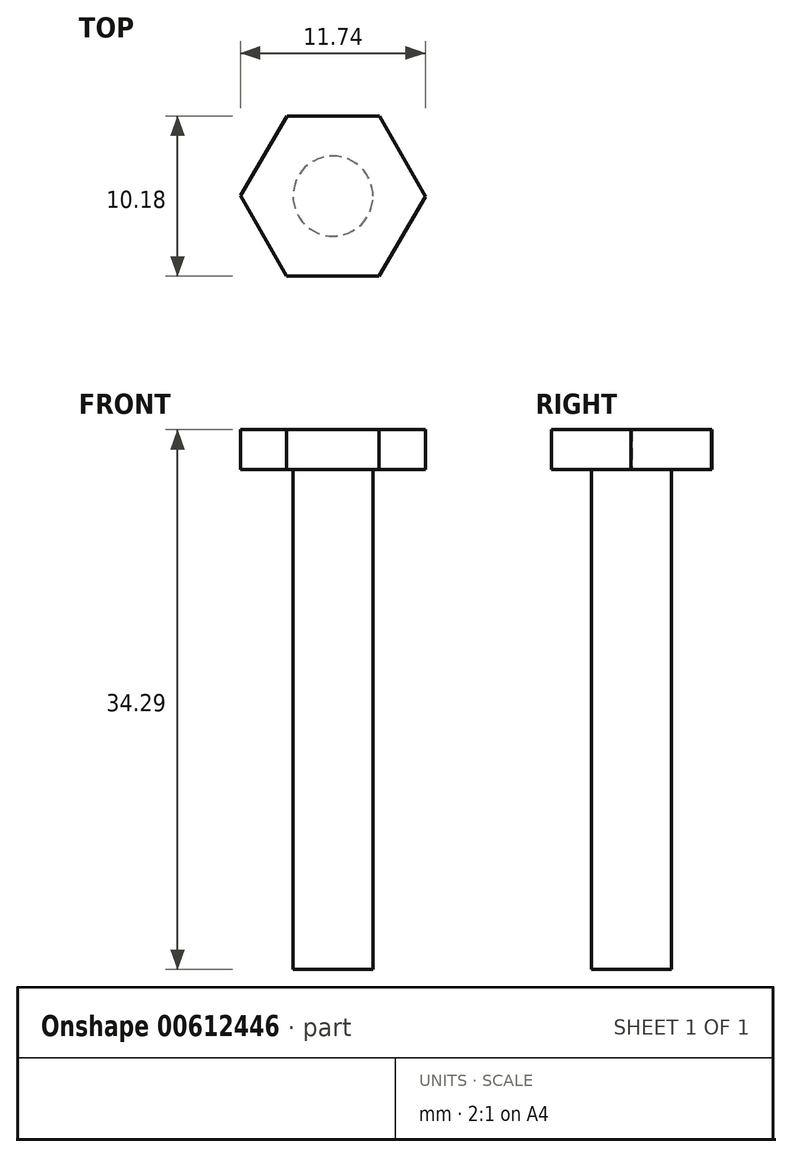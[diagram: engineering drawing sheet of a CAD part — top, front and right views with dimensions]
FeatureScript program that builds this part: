
annotation { "Feature Type Name" : "Feature", "Feature Type Description" : "" }
export const myFeature = defineFeature(function(context is Context, id is Id, definition is map)
    precondition{}
    {
        {
            var Q0;
            Q0=qCreatedBy(makeId("Top.planeOp"),FACE);
            var sketch = newSketch(context, id + "F0", { "sketchPlane" : qUnion([Q0])});
            skCircle(sketch, "E0", {"center": v(0, 0) * mm, "radius": 2.54 * mm});
            skSolve(sketch);
        }
        {
            var Q0;
            Q0 = qSketchRegion(id + "F0", true);
            extrude(context, id + "F1", {"entities" : qUnion([Q0]), "depth" : 31.75 * mm, "offsetDistance" : 25.4 * mm});
        }
        {
            var Q0;
            Q0=makeQuery(id+"F1.opExtrude","CAP_FACE",FACE,{"disambiguationData":[OSD([sQuery(id+"F0.wireOp",EDGE,"E0")])],"isStart":false});
            var sketch = newSketch(context, id + "F2", { "sketchPlane" : qUnion([Q0])});
            skCircle(sketch, "E1.cCircle", {"center": v(0, 0) * mm, "radius": 5.08 * mm, "construction": true});
            skLineSegment(sketch, "E1.0", {"start": v(2.96, 5.07) * mm, "end": v(5.87, -0.03) * mm});
            skLineSegment(sketch, "E1.1", {"start": v(5.87, -0.03) * mm, "end": v(2.9, -5.1) * mm});
            skLineSegment(sketch, "E1.2", {"start": v(2.9, -5.1) * mm, "end": v(-2.96, -5.07) * mm});
            skLineSegment(sketch, "E1.3", {"start": v(-2.96, -5.07) * mm, "end": v(-5.87, 0.03) * mm});
            skLineSegment(sketch, "E1.4", {"start": v(-5.87, 0.03) * mm, "end": v(-2.9, 5.1) * mm});
            skLineSegment(sketch, "E1.5", {"start": v(-2.9, 5.1) * mm, "end": v(2.96, 5.07) * mm});
            skPoint(sketch, "E1.0.midPoint", {"position": v(4.41, 2.52) * mm});
            skSolve(sketch);
        }
        {
            var Q0;
            Q0 = qSketchRegion(id + "F2", true);
            extrude(context, id + "F3", {"entities" : qUnion([Q0]), "operationType" : NewBodyOperationType.ADD, "depth" : 2.54 * mm, "offsetDistance" : 25.4 * mm});
        }
    });
